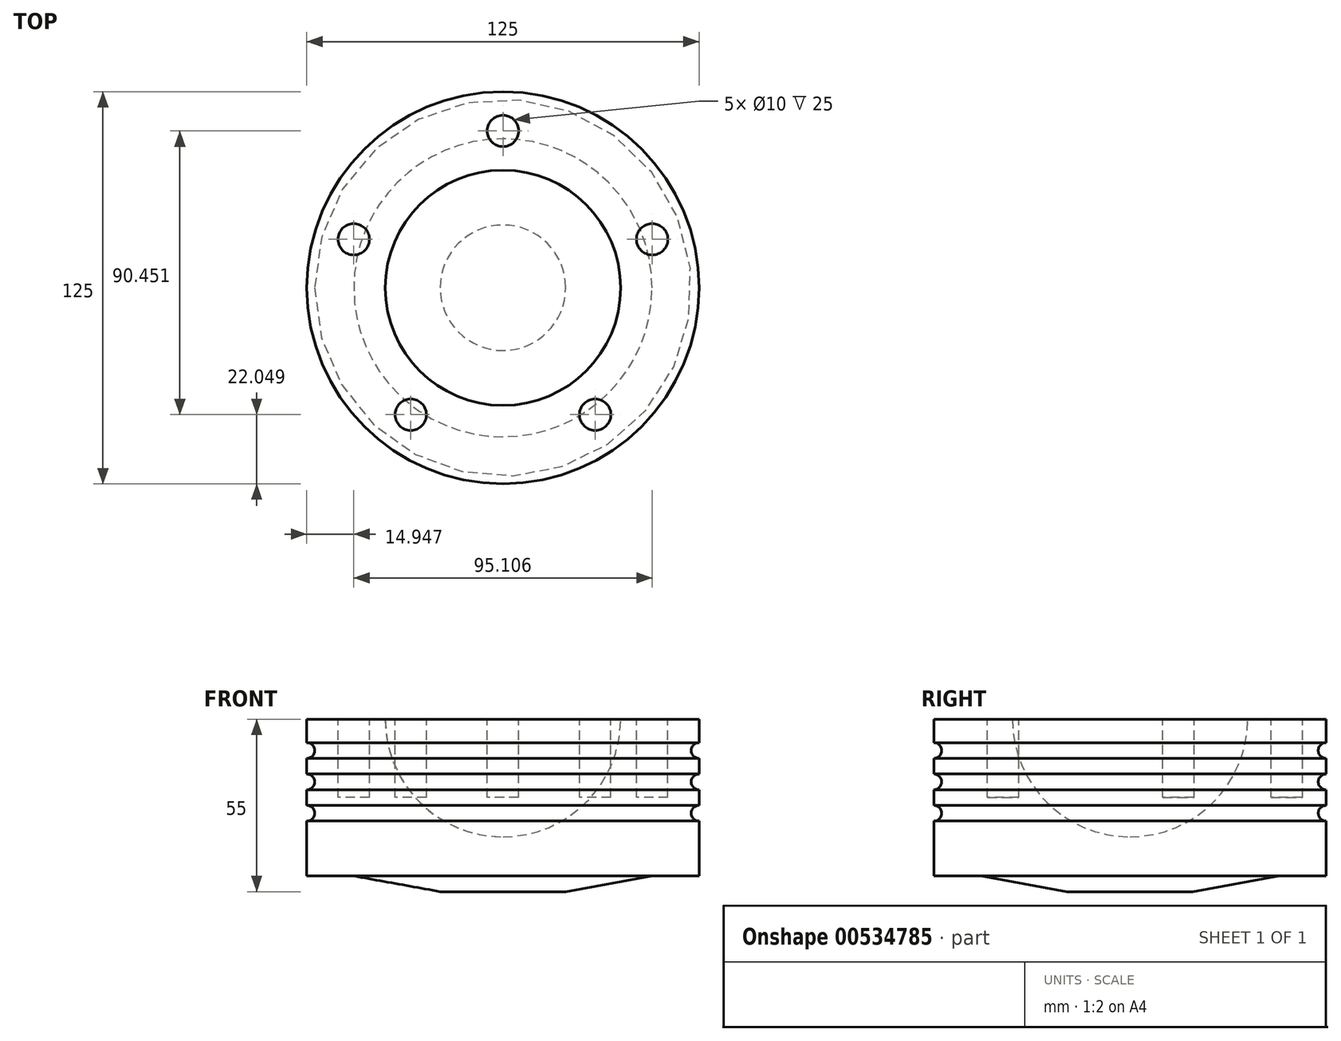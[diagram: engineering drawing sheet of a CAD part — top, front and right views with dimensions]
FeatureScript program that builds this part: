
annotation { "Feature Type Name" : "Feature", "Feature Type Description" : "" }
export const myFeature = defineFeature(function(context is Context, id is Id, definition is map)
    precondition{}
    {
        {
            var Q0;
            Q0=qCreatedBy(makeId("Front.planeOp"),FACE);
            var sketch = newSketch(context, id + "F0", { "sketchPlane" : qUnion([Q0])});
            skLineSegment(sketch, "E0", {"start": v(0, 0) * mm, "end": v(0, 50) * mm});
            skLineSegment(sketch, "E1", {"start": v(0, 50) * mm, "end": v(62.5, 50) * mm});
            skLineSegment(sketch, "E2", {"start": v(62.5, 50) * mm, "end": v(62.5, 0) * mm});
            skLineSegment(sketch, "E3", {"start": v(62.5, 0) * mm, "end": v(47.5, 0) * mm});
            skLineSegment(sketch, "E4", {"start": v(47.5, 0) * mm, "end": v(20, -5) * mm});
            skLineSegment(sketch, "E5", {"start": v(20, -5) * mm, "end": v(0, -5) * mm});
            skLineSegment(sketch, "E6", {"start": v(0, -5) * mm, "end": v(0, 0) * mm});
            skCircle(sketch, "E7", {"center": v(62.5, 20) * mm, "radius": 2.5 * mm});
            skCircle(sketch, "E8.0.1.0", {"center": v(62.5, 30) * mm, "radius": 2.5 * mm});
            skCircle(sketch, "E8.0.2.0", {"center": v(62.5, 40) * mm, "radius": 2.5 * mm});
            skLineSegment(sketch, "E8.direction1", {"start": v(62.5, 20) * mm, "end": v(87.5, 20) * mm, "construction": true});
            skLineSegment(sketch, "E8.direction2", {"start": v(62.5, 20) * mm, "end": v(62.5, 30) * mm, "construction": true});
            skArc(sketch, "E9", {"start": v(37.5, 50) * mm, "mid": v(26.52, 23.48) * mm, "end": v(0, 12.5) * mm});
            skSolve(sketch);
        }
        {
            var Q0;
            {var subQ0=sQuery(id+"F0.wireOp",EDGE,"E3");Q0=makeQuery(id+"F0.imprint","IMPRINT",FACE,{"disambiguationData":[TD([[makeQuery(id+"F0.imprint","IMPRINT",EDGE,{"derivedFrom":subQ0}),-1.0]])]});}
            var Q1;
            {var subQ1=sQuery(id+"F0.wireOp",EDGE,"E1");var subQ3=sQuery(id+"F0.wireOp",EDGE,"hjLFNh8D-WHe6-uvwA-HY3k-wyIB6CZfcN0A");var subQ4=makeQuery(id+"F0.imprint","INTERSECT",VERTEX,{"derivedFrom":[subQ1,subQ3]});Q1=makeQuery(id+"F0.imprint","IMPRINT",FACE,{"disambiguationData":[TD([[makeQuery(id+"F0.imprint","IMPRINT",EDGE,{"disambiguationData":[TD([[subQ4,1.0]])],"derivedFrom":subQ3}),-1.0]])]});}
            var Q2;
            {var subQ0=sQuery(id+"F0.wireOp",EDGE,"uOwqxdfc-jz2v-ZfZa-JEcY-vRitRo0vGmSI");Q2=makeQuery(id+"F0.imprint","IMPRINT",FACE,{"disambiguationData":[TD([[makeQuery(id+"F0.imprint","IMPRINT",EDGE,{"derivedFrom":subQ0}),1.0]])]});}
            var Q3;
            {var subQ0=sQuery(id+"F0.wireOp",EDGE,"uOwqxdfc-jz2v-ZfZa-JEcY-vRitRo0vGmSI");Q3=makeQuery(id+"F0.imprint","IMPRINT",FACE,{"disambiguationData":[TD([[makeQuery(id+"F0.imprint","IMPRINT",EDGE,{"derivedFrom":subQ0}),-1.0]])]});}
            var Q4;
            Q4=sQuery(id+"F0.wireOp",EDGE,"E0");
            revolve(context, id + "F1", {"entities" : qUnion([Q0, Q1, Q2, Q3]), "axis" : qUnion([Q4]), "revolveType" : RevolveType.FULL});
        }
        {
            var Q0;
            Q0=makeQuery(id+"F1.opRevolve","SWEPT_FACE",FACE,{"disambiguationData":[OSD([sQuery(id+"F0.wireOp",EDGE,"E1")])]});
            var sketch = newSketch(context, id + "F2", { "sketchPlane" : qUnion([Q0])});
            skLineSegment(sketch, "E10", {"start": v(0, 37.5) * mm, "end": v(0, 62.5) * mm, "construction": true});
            skCircle(sketch, "E11", {"center": v(0, 50) * mm, "radius": 5 * mm});
            skCircle(sketch, "E12.1.0", {"center": v(-47.55, 15.45) * mm, "radius": 5 * mm});
            skCircle(sketch, "E12.2.0", {"center": v(-29.39, -40.45) * mm, "radius": 5 * mm});
            skCircle(sketch, "E12.3.0", {"center": v(29.39, -40.45) * mm, "radius": 5 * mm});
            skCircle(sketch, "E12.4.0", {"center": v(47.55, 15.45) * mm, "radius": 5 * mm});
            skPoint(sketch, "E12.center", {"position": v(0, 0) * mm});
            skSolve(sketch);
        }
        {
            var Q0;
            Q0 = qSketchRegion(id + "F2", true);
            extrude(context, id + "F3", {"entities" : qUnion([Q0]), "operationType" : NewBodyOperationType.REMOVE, "oppositeDirection" : true, "depth" : 25 * mm, "offsetDistance" : 25 * mm});
        }
    });
